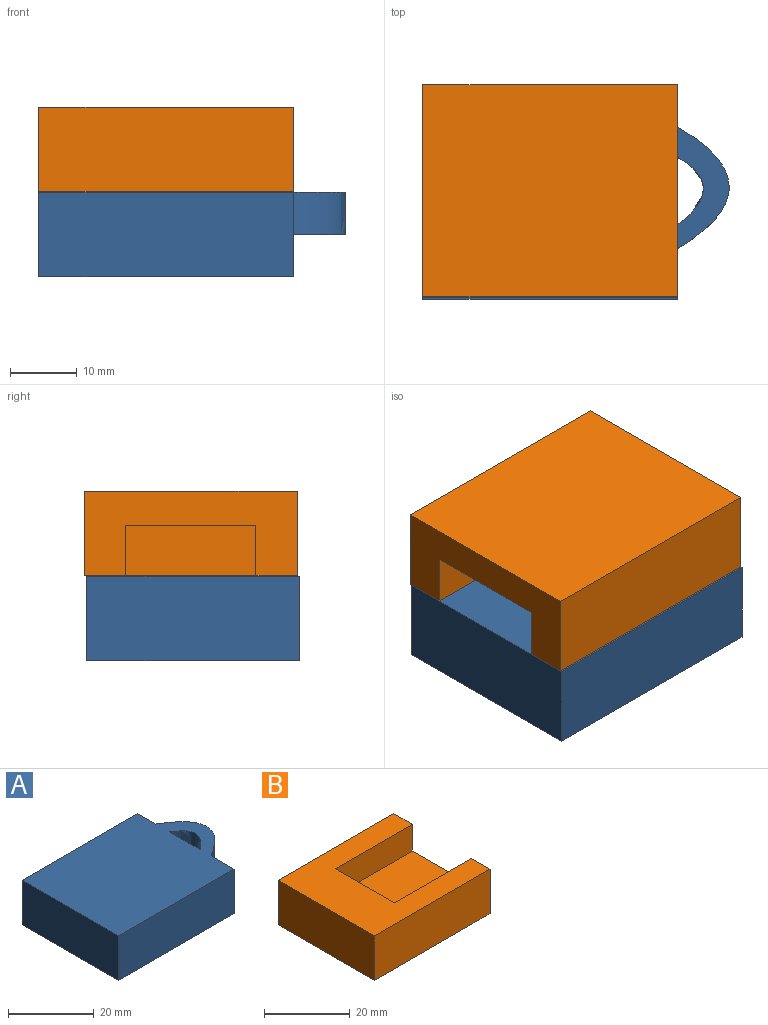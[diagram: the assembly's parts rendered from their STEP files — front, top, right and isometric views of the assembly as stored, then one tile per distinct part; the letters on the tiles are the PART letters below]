
ASSEMBLY  parts=2 mates=1
PART A: 9 faces, bbox 48.7x31.8x12.7 mm
  f0: plane 38.1x12.7mm, normal (0,1,0), area 483.9mm2, adj f1,f3,f4,f5
  f1: plane 31.75x12.7mm, normal (-1,0,0), area 403.2mm2, adj f0,f2,f4,f5
  f2: plane 38.1x12.7mm, normal (0,-1,0), area 483.9mm2, adj f1,f3,f4,f5
  f3: plane 31.75x12.7mm, normal (1,0,0), area 351.6mm2, adj f0,f2,f4,f5,f6,f7,f8
  f4: plane 48.67x31.75mm, normal (0,0,1), area 1277.1mm2, adj f0,f1,f2,f3,f6,f7
  f5: plane 38.1x31.75mm, normal (0,0,-1), area 1209.7mm2, adj f0,f1,f2,f3
  f6: extruded ~18.19x7.69mm, area 157.7mm2, adj f3,f4,f8
  f7: extruded ~10.06x6.35mm, area 83.7mm2, adj f3,f4,f8
  f8: plane 18.19x10.57mm, normal (0,0,-1), area 67.4mm2, adj f3,f6,f7
PART B: 10 faces, bbox 38.1x31.8x12.7 mm
  f0: plane 38.1x31.75mm, normal (0,0,1), area 715.5mm2, adj f1,f2,f3,f4,f7,f8,f9
  f1: plane 38.1x12.7mm, normal (0,1,0), area 483.9mm2, adj f0,f2,f4,f5
  f2: plane 31.75x12.7mm, normal (-1,0,0), area 403.2mm2, adj f0,f1,f3,f5
  f3: plane 38.1x12.7mm, normal (0,-1,0), area 483.9mm2, adj f0,f2,f4,f5
  f4: plane 31.75x12.7mm, normal (1,0,0), area 255mm2, adj f0,f1,f3,f5,f6,f7,f8
  f5: plane 38.1x31.75mm, normal (0,0,-1), area 1209.7mm2, adj f1,f2,f3,f4
  f6: plane 25.4x19.46mm, normal (0,0,1), area 494.2mm2, adj f4,f7,f8,f9
  f7: plane 25.4x7.62mm, normal (0,-1,0), area 193.5mm2, adj f0,f4,f6,f9
  f8: plane 25.4x7.62mm, normal (0,1,0), area 193.5mm2, adj f0,f4,f6,f9
  f9: plane 19.46x7.62mm, normal (1,0,0), area 148.3mm2, adj f0,f6,f7,f8
PLACE A t=(22.46,81.75,-37.42)mm
PLACE B rot(axis=(0,1,0),180deg) t=(22.12,81.08,-12.02)mm
MATE fastened B.f0 <-> A.f4  axis (0,0,-1) through (41.17,81.08,-24.72)mm
